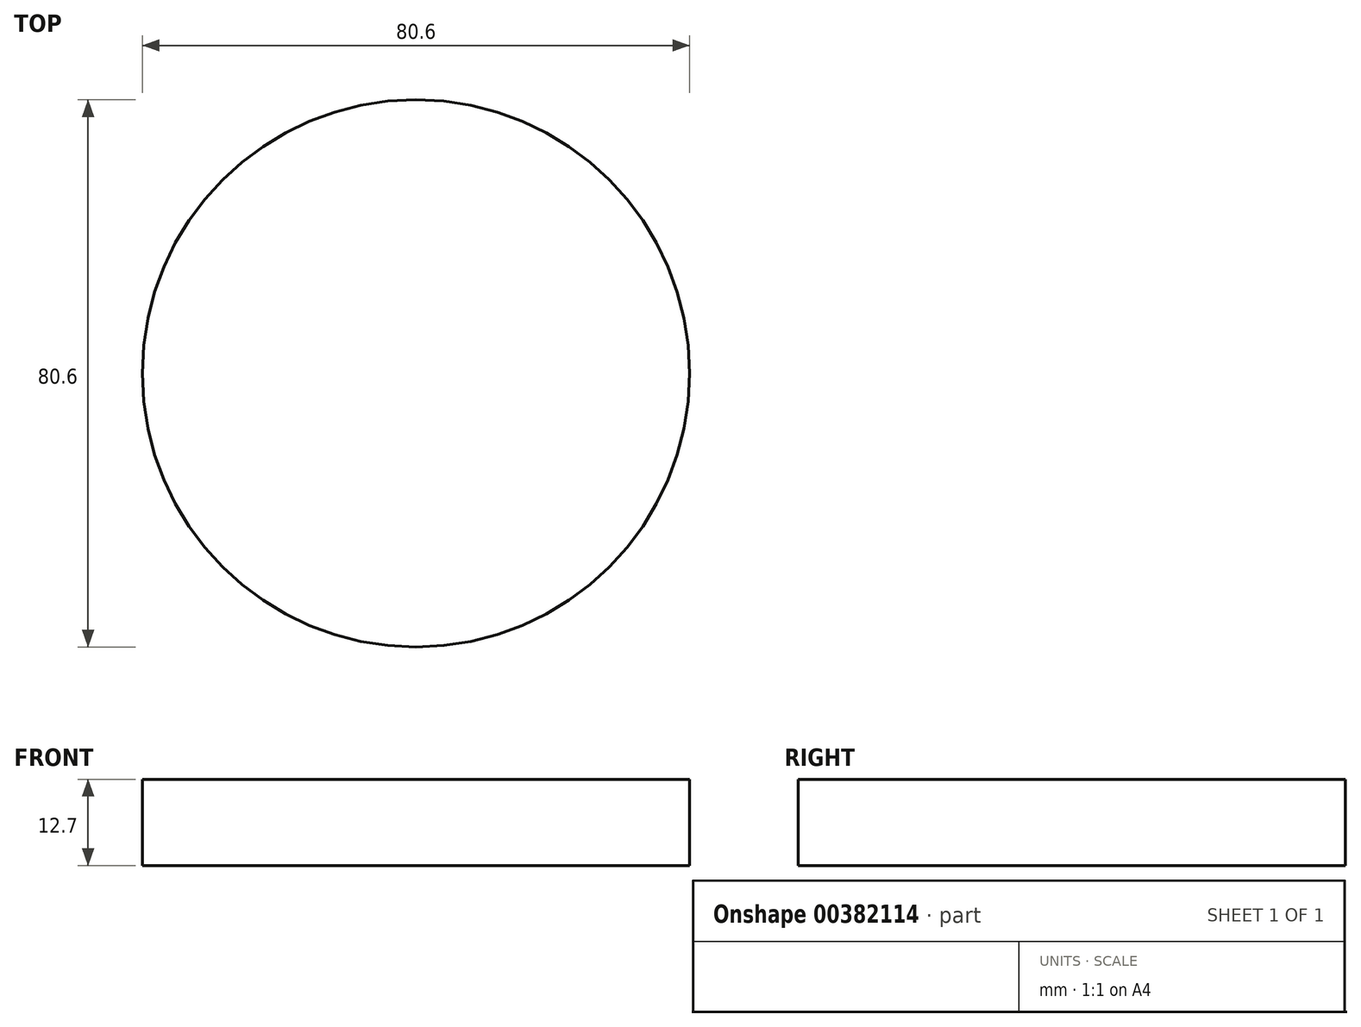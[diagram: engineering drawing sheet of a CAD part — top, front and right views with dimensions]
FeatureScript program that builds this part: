
annotation { "Feature Type Name" : "Feature", "Feature Type Description" : "" }
export const myFeature = defineFeature(function(context is Context, id is Id, definition is map)
    precondition{}
    {
        {
            var Q0;
            Q0=qCreatedBy(makeId("Top.planeOp"),FACE);
            var sketch = newSketch(context, id + "F0", { "sketchPlane" : qUnion([Q0])});
            skCircle(sketch, "E0", {"center": v(12.33, 16.34) * mm, "radius": 40.3 * mm});
            skSolve(sketch);
        }
        {
            var Q0;
            Q0 = qSketchRegion(id + "F0", true);
            extrude(context, id + "F1", {"entities" : qUnion([Q0]), "depth" : 12.7 * mm});
        }
        {
            var Q0;
            Q0=makeQuery(id+"F1.opExtrude","CAP_FACE",FACE,{"disambiguationData":[OSD([sQuery(id+"F0.wireOp",EDGE,"E0")])],"isStart":false});
            var sketch = newSketch(context, id + "F2", { "sketchPlane" : qUnion([Q0])});
            skLineSegment(sketch, "E1", {"start": v(12.33, 16.34) * mm, "end": v(44.64, 40.42) * mm});
            skLineSegment(sketch, "E2.1.0", {"start": v(12.33, 16.34) * mm, "end": v(21.6, 55.56) * mm});
            skLineSegment(sketch, "E2.2.0", {"start": v(12.33, 16.34) * mm, "end": v(-5.77, 52.34) * mm});
            skLineSegment(sketch, "E2.3.0", {"start": v(12.33, 16.34) * mm, "end": v(-24.68, 32.28) * mm});
            skLineSegment(sketch, "E2.4.0", {"start": v(12.33, 16.34) * mm, "end": v(-26.27, 4.76) * mm});
            skLineSegment(sketch, "E2.5.0", {"start": v(12.33, 16.34) * mm, "end": v(-9.8, -17.34) * mm});
            skLineSegment(sketch, "E2.6.0", {"start": v(12.33, 16.34) * mm, "end": v(17.03, -23.69) * mm});
            skLineSegment(sketch, "E2.7.0", {"start": v(12.33, 16.34) * mm, "end": v(41.66, -11.3) * mm});
            skLineSegment(sketch, "E2.8.0", {"start": v(12.33, 16.34) * mm, "end": v(52.56, 14.01) * mm});
            skPoint(sketch, "E2.center", {"position": v(12.33, 16.34) * mm});
            skSolve(sketch);
        }
        {
            var Q0;
            Q0=sQuery(id+"F2.wireOp",EDGE,"E1");
            extrude(context, id + "F3", {"bodyType" : ToolBodyType.SURFACE, "surfaceEntities" : qUnion([Q0]), "oppositeDirection" : true, "depth" : 2.54 * mm});
        }
        {
            var Q0;
            Q0=sQuery(id+"F2.wireOp",EDGE,"E2.1.0");
            extrude(context, id + "F4", {"bodyType" : ToolBodyType.SURFACE, "surfaceEntities" : qUnion([Q0]), "oppositeDirection" : true, "depth" : 2.54 * mm});
        }
        {
            var Q0;
            Q0=sQuery(id+"F2.wireOp",EDGE,"E2.2.0");
            extrude(context, id + "F5", {"bodyType" : ToolBodyType.SURFACE, "surfaceEntities" : qUnion([Q0]), "oppositeDirection" : true, "depth" : 2.54 * mm});
        }
        {
            var Q0;
            Q0=sQuery(id+"F2.wireOp",EDGE,"E2.3.0");
            extrude(context, id + "F6", {"bodyType" : ToolBodyType.SURFACE, "surfaceEntities" : qUnion([Q0]), "oppositeDirection" : true, "depth" : 2.54 * mm});
        }
        {
            var Q0;
            Q0=sQuery(id+"F2.wireOp",EDGE,"E2.4.0");
            extrude(context, id + "F7", {"bodyType" : ToolBodyType.SURFACE, "surfaceEntities" : qUnion([Q0]), "oppositeDirection" : true, "depth" : 2.54 * mm});
        }
        {
            var Q0;
            Q0=sQuery(id+"F2.wireOp",EDGE,"E2.5.0");
            extrude(context, id + "F8", {"bodyType" : ToolBodyType.SURFACE, "surfaceEntities" : qUnion([Q0]), "oppositeDirection" : true, "depth" : 2.54 * mm});
        }
        {
            var Q0;
            Q0=sQuery(id+"F2.wireOp",EDGE,"E2.6.0");
            extrude(context, id + "F9", {"bodyType" : ToolBodyType.SURFACE, "surfaceEntities" : qUnion([Q0]), "oppositeDirection" : true, "depth" : 2.54 * mm});
        }
        {
            var Q0;
            Q0=sQuery(id+"F2.wireOp",EDGE,"E2.7.0");
            extrude(context, id + "F10", {"bodyType" : ToolBodyType.SURFACE, "surfaceEntities" : qUnion([Q0]), "oppositeDirection" : true, "depth" : 2.54 * mm});
        }
    });
